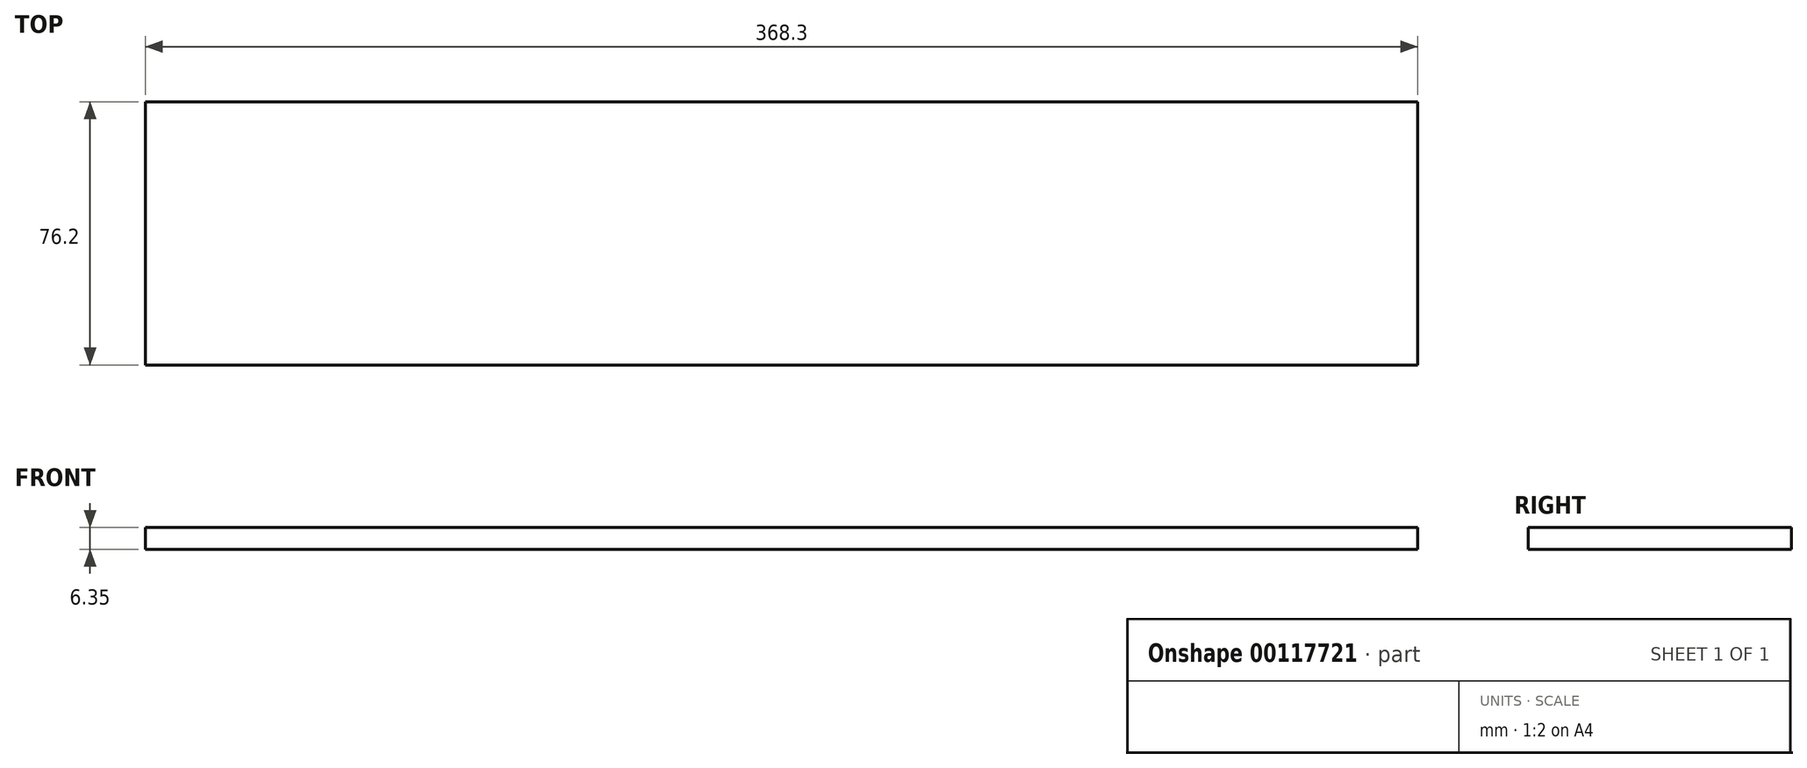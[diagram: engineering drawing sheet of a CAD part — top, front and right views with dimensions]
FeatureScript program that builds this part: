
annotation { "Feature Type Name" : "Feature", "Feature Type Description" : "" }
export const myFeature = defineFeature(function(context is Context, id is Id, definition is map)
    precondition{}
    {
        {
            var Q0;
            Q0=qCreatedBy(makeId("Top.planeOp"),FACE);
            var sketch = newSketch(context, id + "F0", { "sketchPlane" : qUnion([Q0])});
            skLineSegment(sketch, "E0.bottom", {"start": v(-177.9, 26.28) * mm, "end": v(190.4, 26.28) * mm});
            skLineSegment(sketch, "E0.top", {"start": v(-177.9, -49.92) * mm, "end": v(190.4, -49.92) * mm});
            skLineSegment(sketch, "E0.left", {"start": v(-177.9, 26.28) * mm, "end": v(-177.9, -49.92) * mm});
            skLineSegment(sketch, "E0.right", {"start": v(190.4, 26.28) * mm, "end": v(190.4, -49.92) * mm});
            skSolve(sketch);
        }
        {
            var Q0;
            Q0 = qSketchRegion(id + "F0", true);
            extrude(context, id + "F1", {"entities" : qUnion([Q0]), "depth" : 6.35 * mm});
        }
    });
